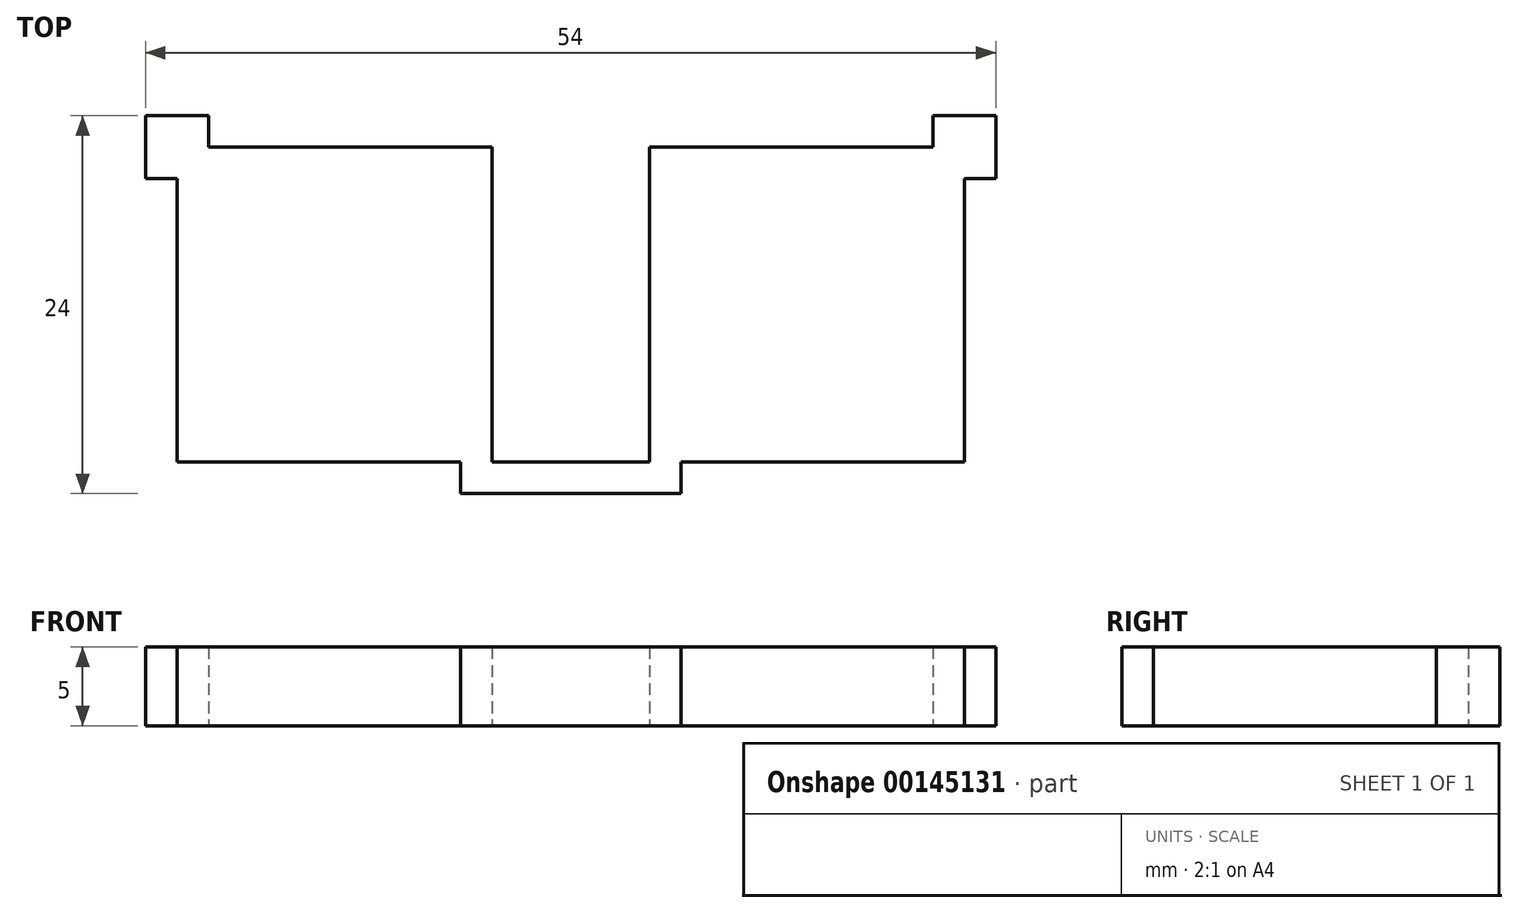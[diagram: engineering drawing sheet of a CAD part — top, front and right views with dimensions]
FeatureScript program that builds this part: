
annotation { "Feature Type Name" : "Feature", "Feature Type Description" : "" }
export const myFeature = defineFeature(function(context is Context, id is Id, definition is map)
    precondition{}
    {
        {
            var Q0;
            Q0=qCreatedBy(makeId("Top.planeOp"),FACE);
            var sketch = newSketch(context, id + "F0", { "sketchPlane" : qUnion([Q0])});
            skLineSegment(sketch, "E0", {"start": v(0, 0) * mm, "end": v(5, 0) * mm});
            skLineSegment(sketch, "E1.bottom", {"start": v(5, 0) * mm, "end": v(25, 0) * mm});
            skLineSegment(sketch, "E1.top", {"start": v(5, 20) * mm, "end": v(25, 20) * mm});
            skLineSegment(sketch, "E1.left", {"start": v(5, 0) * mm, "end": v(5, 20) * mm});
            skLineSegment(sketch, "E1.right", {"start": v(25, 0) * mm, "end": v(25, 20) * mm});
            skLineSegment(sketch, "E2", {"start": v(23, 20) * mm, "end": v(23, 22) * mm});
            skLineSegment(sketch, "E3", {"start": v(23, 22) * mm, "end": v(27, 22) * mm});
            skLineSegment(sketch, "E4", {"start": v(27, 22) * mm, "end": v(27, 18) * mm});
            skLineSegment(sketch, "E5", {"start": v(27, 18) * mm, "end": v(25, 18) * mm});
            skLineSegment(sketch, "E6", {"start": v(7, 0) * mm, "end": v(7, -2) * mm});
            skLineSegment(sketch, "E7", {"start": v(7, -2) * mm, "end": v(0, -2) * mm});
            skLineSegment(sketch, "E8", {"start": v(0, 0) * mm, "end": v(0, 7.54) * mm, "construction": true});
            skLineSegment(sketch, "E9.MirrorCS", {"start": v(0, 0) * mm, "end": v(-5, 0) * mm});
            skLineSegment(sketch, "E10.MirrorCS", {"start": v(-5, 0) * mm, "end": v(-25, 0) * mm});
            skLineSegment(sketch, "E11.MirrorCS", {"start": v(-7, 0) * mm, "end": v(-7, -2) * mm});
            skLineSegment(sketch, "E12.MirrorCS", {"start": v(-7, -2) * mm, "end": v(0, -2) * mm});
            skLineSegment(sketch, "E13.MirrorCS", {"start": v(-5, 20) * mm, "end": v(-25, 20) * mm});
            skLineSegment(sketch, "E14.MirrorCS", {"start": v(-27, 18) * mm, "end": v(-25, 18) * mm});
            skLineSegment(sketch, "E15.MirrorCS", {"start": v(-5, 0) * mm, "end": v(-5, 20) * mm});
            skLineSegment(sketch, "E16.MirrorCS", {"start": v(-25, 0) * mm, "end": v(-25, 20) * mm});
            skLineSegment(sketch, "E17.MirrorCS", {"start": v(-23, 20) * mm, "end": v(-23, 22) * mm});
            skLineSegment(sketch, "E18.MirrorCS", {"start": v(-23, 22) * mm, "end": v(-27, 22) * mm});
            skLineSegment(sketch, "E19.MirrorCS", {"start": v(-27, 22) * mm, "end": v(-27, 18) * mm});
            skSolve(sketch);
        }
        {
            var Q0;
            Q0 = qSketchRegion(id + "F0", true);
            extrude(context, id + "F1", {"entities" : qUnion([Q0]), "depth" : 5 * mm});
        }
    });
